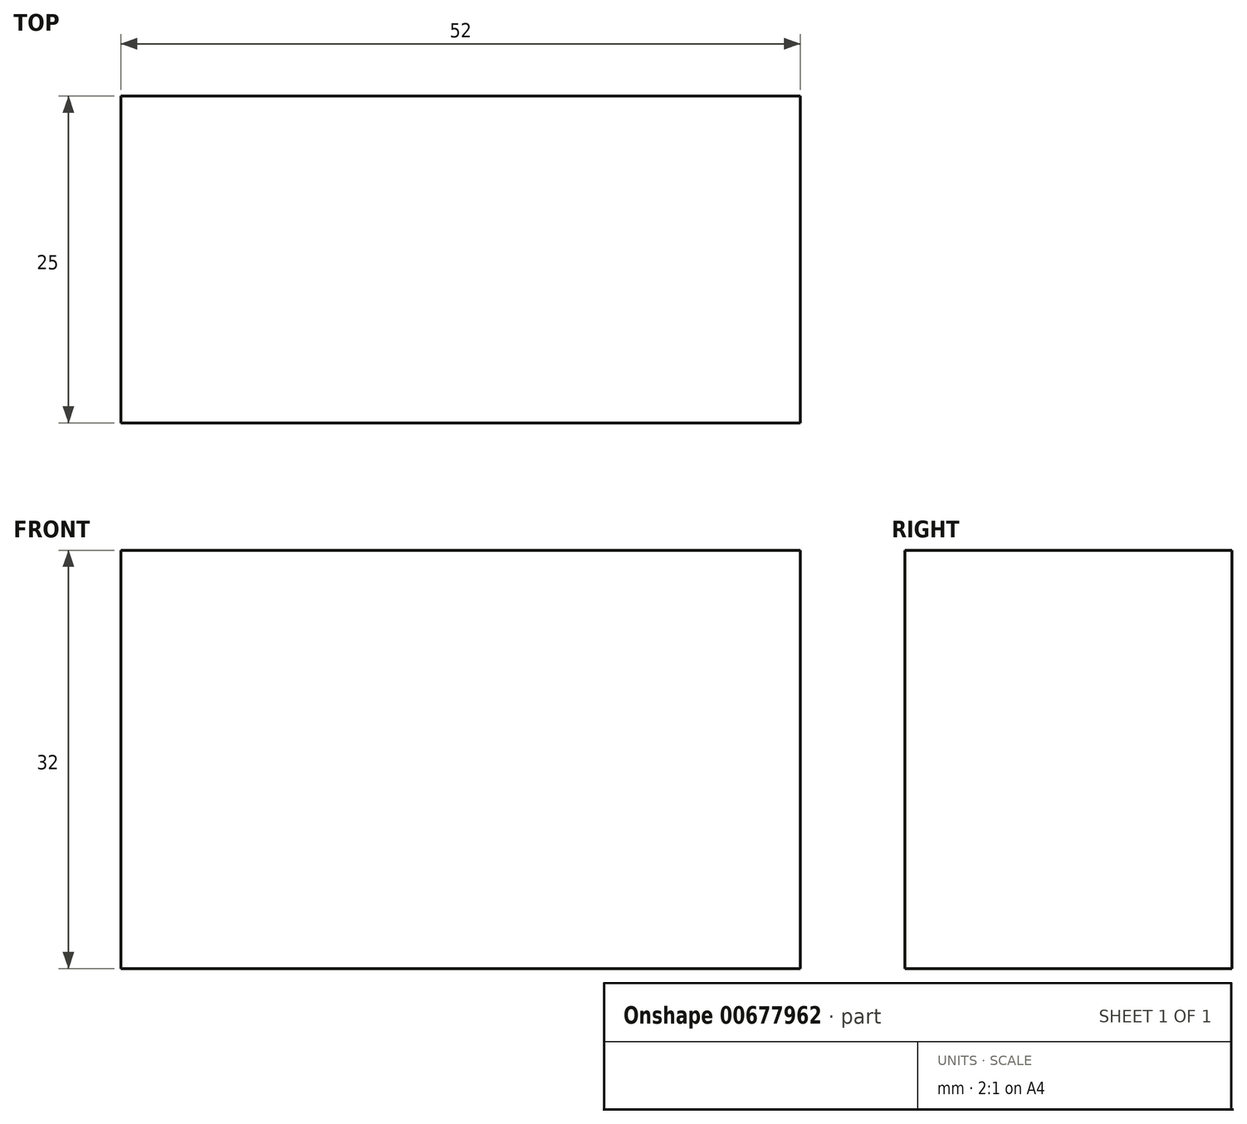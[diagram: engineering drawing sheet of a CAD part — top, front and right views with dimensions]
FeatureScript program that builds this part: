
annotation { "Feature Type Name" : "Feature", "Feature Type Description" : "" }
export const myFeature = defineFeature(function(context is Context, id is Id, definition is map)
    precondition{}
    {
        {
            var Q0;
            Q0=qCreatedBy(makeId("Front.planeOp"),FACE);
            var sketch = newSketch(context, id + "F0", { "sketchPlane" : qUnion([Q0])});
            skLineSegment(sketch, "E0.bottom", {"start": v(0, 0) * mm, "end": v(52, 0) * mm});
            skLineSegment(sketch, "E0.top", {"start": v(0, 32) * mm, "end": v(52, 32) * mm});
            skLineSegment(sketch, "E0.left", {"start": v(0, 0) * mm, "end": v(0, 32) * mm});
            skLineSegment(sketch, "E0.right", {"start": v(52, 0) * mm, "end": v(52, 32) * mm});
            skSolve(sketch);
        }
        {
            var Q0;
            Q0 = qSketchRegion(id + "F0", true);
            extrude(context, id + "F1", {"entities" : qUnion([Q0]), "depth" : 25 * mm, "offsetDistance" : 25 * mm});
        }
    });
